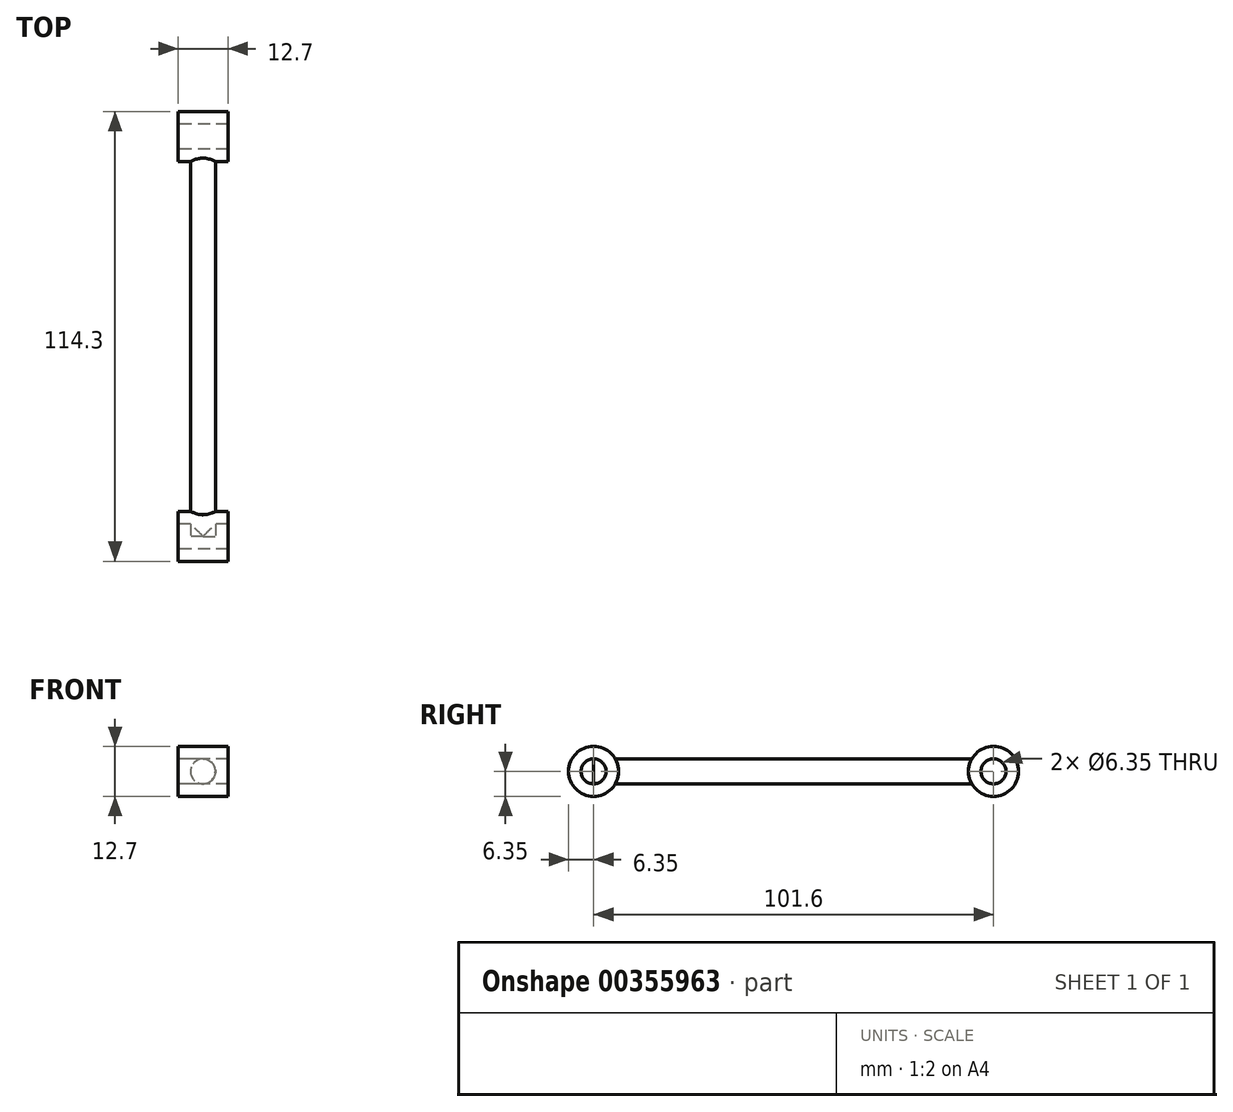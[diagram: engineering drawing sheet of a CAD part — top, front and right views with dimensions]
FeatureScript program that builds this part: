
annotation { "Feature Type Name" : "Feature", "Feature Type Description" : "" }
export const myFeature = defineFeature(function(context is Context, id is Id, definition is map)
    precondition{}
    {
        {
            var Q0;
            Q0=qCreatedBy(makeId("Right.planeOp"),FACE);
            var sketch = newSketch(context, id + "F0", { "sketchPlane" : qUnion([Q0])});
            skCircle(sketch, "E0", {"center": v(0, 0) * mm, "radius": 3.18 * mm});
            skLineSegment(sketch, "E1", {"start": v(0, 0) * mm, "end": v(101.6, 0) * mm, "construction": true});
            skCircle(sketch, "E2", {"center": v(101.6, 0) * mm, "radius": 3.18 * mm});
            skCircle(sketch, "E3", {"center": v(0, 0) * mm, "radius": 6.35 * mm});
            skCircle(sketch, "E4", {"center": v(101.6, 0) * mm, "radius": 6.35 * mm});
            skSolve(sketch);
        }
        {
            var Q0;
            Q0=qCreatedBy(makeId("Front.planeOp"),FACE);
            var sketch = newSketch(context, id + "F1", { "sketchPlane" : qUnion([Q0])});
            skCircle(sketch, "E5", {"center": v(0, 0) * mm, "radius": 3.18 * mm});
            skSolve(sketch);
        }
        {
            var Q0;
            Q0=qSketchRegion(id+"F0",true);
            extrude(context, id + "F2", {"entities" : qUnion([Q0]), "endBound" : BoundingType.SYMMETRIC, "depth" : 12.7 * mm});
        }
        {
            var Q0;
            Q0=qSketchRegion(id+"F1",true);
            var Q1;
            Q1=makeQuery(id+"F2.opExtrude","SWEPT_FACE",FACE,{"disambiguationData":[OSD([sQuery(id+"F0.wireOp",EDGE,"E4")])]});
            extrude(context, id + "F3", {"entities" : qUnion([Q0]), "operationType" : NewBodyOperationType.ADD, "endBound" : BoundingType.UP_TO_SURFACE, "oppositeDirection" : true, "endBoundEntityFace" : qUnion([Q1]), "depth" : 25.4 * mm});
        }
    });
